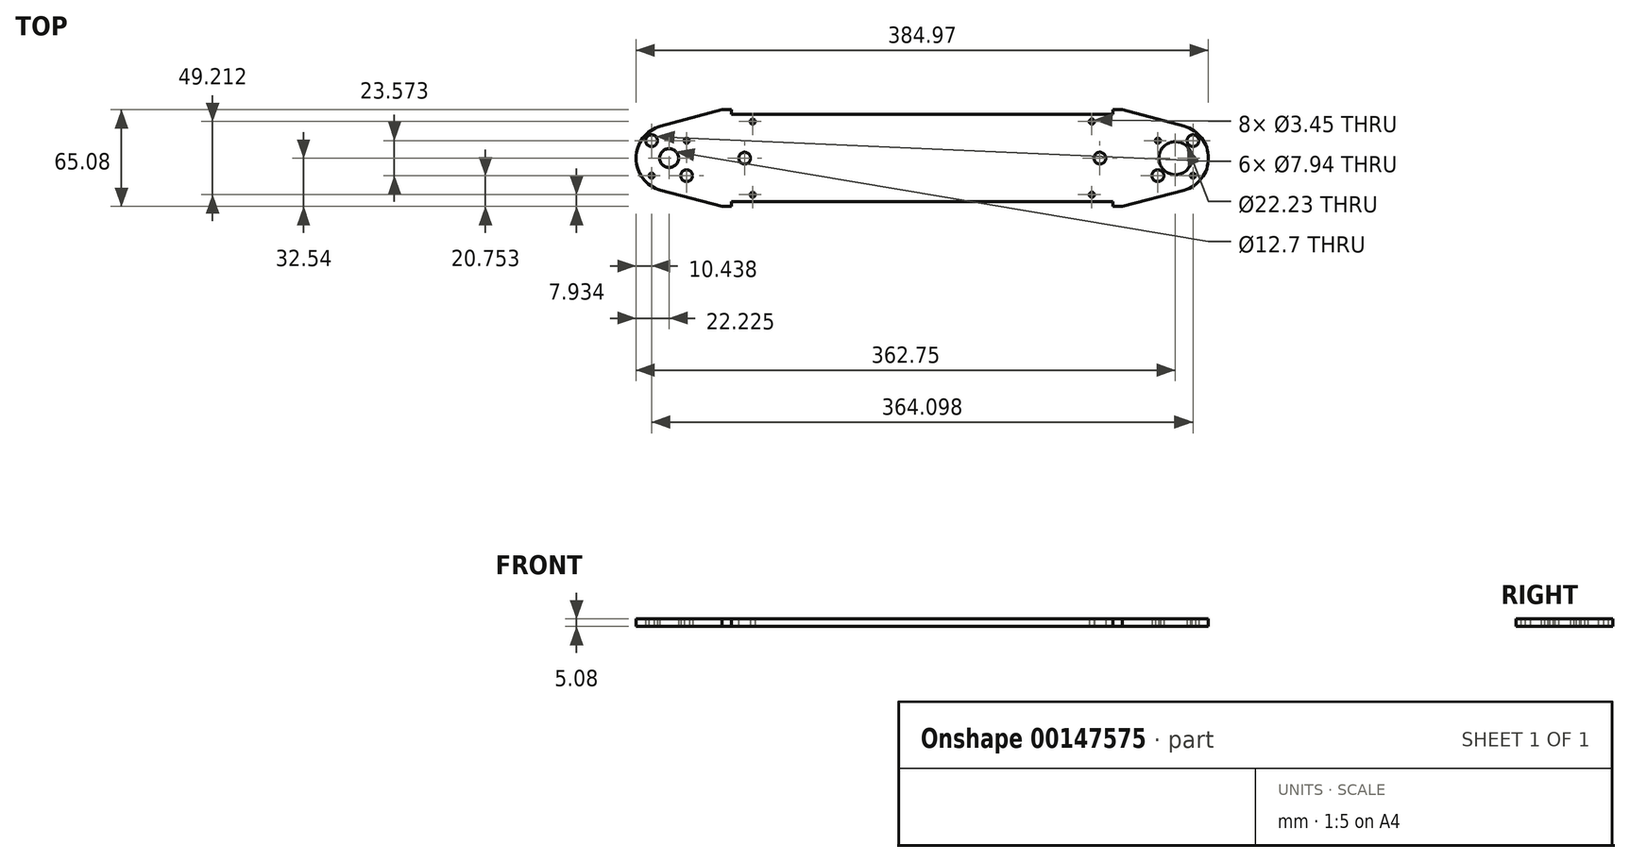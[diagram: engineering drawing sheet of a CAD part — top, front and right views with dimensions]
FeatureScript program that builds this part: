
annotation { "Feature Type Name" : "Feature", "Feature Type Description" : "" }
export const myFeature = defineFeature(function(context is Context, id is Id, definition is map)
    precondition{}
    {
        {
            var Q0;
            Q0=qCreatedBy(makeId("Top.planeOp"),FACE);
            var sketch = newSketch(context, id + "F0", { "sketchPlane" : qUnion([Q0])});
            skPoint(sketch, "E0.rect.middle", {"position": v(0, 0) * mm});
            skCircle(sketch, "E1", {"center": v(0, 0) * mm, "radius": 11.11 * mm});
            skLineSegment(sketch, "E2.bottom", {"start": v(11.79, 11.79) * mm, "end": v(-11.79, 11.79) * mm, "construction": true});
            skLineSegment(sketch, "E2.left", {"start": v(11.79, 11.79) * mm, "end": v(11.79, -11.79) * mm, "construction": true});
            skLineSegment(sketch, "E2.right", {"start": v(-11.79, 11.79) * mm, "end": v(-11.79, -11.79) * mm, "construction": true});
            skCircle(sketch, "E3", {"center": v(11.79, 11.79) * mm, "radius": 5.56 * mm, "construction": true});
            skCircle(sketch, "E4", {"center": v(-11.79, 11.79) * mm, "radius": 1.73 * mm});
            skCircle(sketch, "E5", {"center": v(11.79, 11.79) * mm, "radius": 3.97 * mm});
            skCircle(sketch, "E6", {"center": v(11.79, -11.79) * mm, "radius": 1.73 * mm});
            skCircle(sketch, "E7", {"center": v(-11.79, -11.79) * mm, "radius": 3.97 * mm});
            skArc(sketch, "E8", {"start": v(-346.28, 21.47) * mm, "mid": v(-362.75, 0) * mm, "end": v(-346.28, -21.47) * mm});
            skLineSegment(sketch, "E9.bottom", {"start": v(-352.31, 11.79) * mm, "end": v(-328.74, 11.79) * mm, "construction": true});
            skLineSegment(sketch, "E9.top", {"start": v(-352.31, -11.79) * mm, "end": v(-328.74, -11.79) * mm, "construction": true});
            skLineSegment(sketch, "E9.left", {"start": v(-352.31, 11.79) * mm, "end": v(-352.31, -11.79) * mm, "construction": true});
            skLineSegment(sketch, "E9.right", {"start": v(-328.74, 11.79) * mm, "end": v(-328.74, -11.79) * mm, "construction": true});
            skCircle(sketch, "E10", {"center": v(-328.74, 11.79) * mm, "radius": 1.73 * mm});
            skCircle(sketch, "E11", {"center": v(-340.53, 0) * mm, "radius": 6.35 * mm});
            skCircle(sketch, "E12", {"center": v(-352.31, 11.79) * mm, "radius": 3.97 * mm});
            skCircle(sketch, "E13", {"center": v(-352.31, -11.79) * mm, "radius": 1.73 * mm});
            skCircle(sketch, "E14", {"center": v(-328.74, -11.79) * mm, "radius": 3.97 * mm});
            skLineSegment(sketch, "E15", {"start": v(0, 0) * mm, "end": v(-340.53, 0) * mm, "construction": true});
            skLineSegment(sketch, "E16", {"start": v(-346.28, -21.47) * mm, "end": v(-304.94, -32.54) * mm});
            skLineSegment(sketch, "E17", {"start": v(-346.28, 21.47) * mm, "end": v(-304.94, 32.54) * mm});
            skLineSegment(sketch, "E18", {"start": v(-298.6, -29.37) * mm, "end": v(-41.93, -29.37) * mm});
            skLineSegment(sketch, "E19", {"start": v(-298.6, 29.37) * mm, "end": v(-41.93, 29.37) * mm});
            skLineSegment(sketch, "E20", {"start": v(-298.6, 32.54) * mm, "end": v(-298.6, 29.37) * mm});
            skLineSegment(sketch, "E21", {"start": v(-298.6, 32.54) * mm, "end": v(-304.94, 32.54) * mm});
            skLineSegment(sketch, "E22", {"start": v(-298.6, -29.37) * mm, "end": v(-298.6, -32.54) * mm});
            skLineSegment(sketch, "E23", {"start": v(-298.6, -32.54) * mm, "end": v(-304.94, -32.54) * mm});
            skLineSegment(sketch, "E24", {"start": v(-41.93, -29.37) * mm, "end": v(-41.93, -32.54) * mm});
            skLineSegment(sketch, "E25", {"start": v(-41.93, -32.54) * mm, "end": v(-35.58, -32.54) * mm});
            skLineSegment(sketch, "E26", {"start": v(-41.93, 29.37) * mm, "end": v(-41.93, 32.54) * mm});
            skLineSegment(sketch, "E27", {"start": v(-41.93, 32.54) * mm, "end": v(-35.58, 32.54) * mm});
            skLineSegment(sketch, "E28", {"start": v(-35.58, -32.54) * mm, "end": v(5.75, -21.47) * mm});
            skLineSegment(sketch, "E29", {"start": v(5.75, 21.47) * mm, "end": v(-35.58, 32.54) * mm});
            skArc(sketch, "E30", {"start": v(5.75, -21.47) * mm, "mid": v(22.23, 0) * mm, "end": v(5.75, 21.47) * mm});
            skLineSegment(sketch, "E31", {"start": v(-298.6, 29.37) * mm, "end": v(-298.6, 24.6) * mm, "construction": true});
            skLineSegment(sketch, "E32", {"start": v(-298.6, 24.6) * mm, "end": v(-284.3, 24.6) * mm, "construction": true});
            skLineSegment(sketch, "E33", {"start": v(-298.6, -29.37) * mm, "end": v(-298.6, -24.6) * mm, "construction": true});
            skLineSegment(sketch, "E34", {"start": v(-298.6, -24.6) * mm, "end": v(-284.3, -24.6) * mm, "construction": true});
            skLineSegment(sketch, "E35", {"start": v(-41.93, -29.37) * mm, "end": v(-41.93, -24.6) * mm, "construction": true});
            skLineSegment(sketch, "E36", {"start": v(-41.93, -24.6) * mm, "end": v(-56.22, -24.6) * mm, "construction": true});
            skLineSegment(sketch, "E37", {"start": v(-41.93, 29.37) * mm, "end": v(-41.93, 24.6) * mm, "construction": true});
            skLineSegment(sketch, "E38", {"start": v(-41.93, 24.6) * mm, "end": v(-56.22, 24.6) * mm, "construction": true});
            skCircle(sketch, "E39", {"center": v(-284.3, 24.6) * mm, "radius": 1.73 * mm});
            skCircle(sketch, "E40", {"center": v(-56.22, 24.6) * mm, "radius": 1.73 * mm});
            skCircle(sketch, "E41", {"center": v(-56.22, -24.6) * mm, "radius": 1.73 * mm});
            skCircle(sketch, "E42", {"center": v(-284.3, -24.6) * mm, "radius": 1.73 * mm});
            skLineSegment(sketch, "E43", {"start": v(-11.79, -11.79) * mm, "end": v(11.79, -11.79) * mm, "construction": true});
            skLineSegment(sketch, "E44", {"start": v(-170.26, -29.37) * mm, "end": v(-170.26, 0) * mm, "construction": true});
            skLineSegment(sketch, "E45", {"start": v(-170.26, 0) * mm, "end": v(-170.26, 29.37) * mm, "construction": true});
            skLineSegment(sketch, "E46", {"start": v(-328.74, 11.79) * mm, "end": v(-289.73, 11.79) * mm, "construction": true});
            skLineSegment(sketch, "E47", {"start": v(-289.73, 11.79) * mm, "end": v(-289.73, 0) * mm, "construction": true});
            skLineSegment(sketch, "E48", {"start": v(-11.79, 11.79) * mm, "end": v(-50.8, 11.79) * mm, "construction": true});
            skLineSegment(sketch, "E49", {"start": v(-50.8, 11.79) * mm, "end": v(-50.8, 0) * mm, "construction": true});
            skCircle(sketch, "E50", {"center": v(-50.8, 0) * mm, "radius": 3.97 * mm});
            skCircle(sketch, "E51", {"center": v(-289.73, 0) * mm, "radius": 3.97 * mm});
            skLineSegment(sketch, "E52", {"start": v(5.75, 21.47) * mm, "end": v(-14.92, 21.47) * mm, "construction": true});
            skLineSegment(sketch, "E53", {"start": v(-14.92, 21.47) * mm, "end": v(-14.92, 27) * mm, "construction": true});
            skSolve(sketch);
        }
        {
            var Q0;
            Q0=qSketchRegion(id+"F0",true);
            extrude(context, id + "F1", {"entities" : qUnion([Q0]), "depth" : 5.08 * mm});
        }
    });
